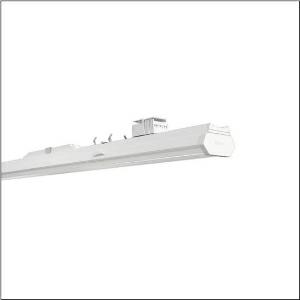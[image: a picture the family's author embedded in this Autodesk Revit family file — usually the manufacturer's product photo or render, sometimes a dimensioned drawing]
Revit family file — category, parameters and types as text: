
# Revit family: licross_r__11_protected_mo_51td12dn495g3s_4e23
name_source: partatom
category: Lighting Fixtures
units: mm (PartAtom-declared; Revit-internal decimal feet)

## family parameters
Cut with Voids When Loaded = No
Host = Face
Light Source = No
Part Type = Normal
Room Calculation Point = No
Round Connector Dimension = Use Diameter
Shared = No

## types (1)
- --- (1 x LED, 980 lm, 6.8 W, 4000K)
    Apparent Load = 7 VA
    CIE Flux Codes = 73 92 98 99 100
    Color Rendering = 80
    Color Temperature = 4000K
    Default Elevation = 1800 mm
    Description = Licross® 11 Protected MO, luminaire insert, of sheet steel, galvanised, coil coated, white, length: 1.500mm, width: 90mm, height: 101mm, LED rated luminous flux: 9.980lm, light colour: 840, control gear: DALI 2 (for two DALI lines), with plug, 6-pole, with phase selection, for trunking rail, 14-core, mains connection: 220..240V, AC, 50/60Hz, rated input power: 61W, for trunking rail, 14-core, halogen-free wiring, for emergency light function, converter,control gear: single battery element, battery: LiFePO4, 9Ah, primary light control with lens, of plastic, primary optical cover: cover, of PMMA, light emission: direct distribution, primary light characteristic: symmetric, protection rating (complete): IP54, insulation class (complete): insulation class I (protective earthing), certification: CE, UKCA, protection symbol: D if used in an environment with non-conductive dust loads with corresponding accessories, impact resistance: IK06, permissible ambient temperature for indoor applications: +5..+35°C, standard: EN 60598-2-22, LABS conformity tested according to VDMA 24364:2018-05, reducing of maximum allowable ambient temperature of 5°C with ceiling mounting, corresponds to IFS (International Featured Standards) requirements for safety and quality in the food industry, packaging unit: 1 piece
    Height = 92 mm
    Lamp = 1 x LED
    Lamp Light Flux = 980 lm
    Lamp Power = 6.8 W
    Lamp count = 1
    Length = 1500 mm
    Luminous efficacy = 144 lm/W
    Manufacturer = Siteco
    ModVariant = No
    Model = 51TD12DN495G3S
    Mounting Place = Ceiling
    Mounting Type = Pendant
    Number of Poles = 1
    OnlyDefault = Yes
    Power Factor = 1
    Product Name = Licross® 11 Protected MO
    Product group = luminaire insert
    ProductGroupID = 902
    Protection Class = Protection class I
    Protection Degree = IP 54
    RLX_Detail_Level = 1
    RLX_Emergency_Light_Flux = 0 lm
    RLX_Emergency_Type = 0
    RLX_Emergency_Type_DB = No
    RlxData = <blob elided: 24801 chars, md5=7ffff361>
    Socket = socket
    Standby Power = 0 W
    System Light Flux = 980 lm
    System Power = 7 W
    Type Comments = : emergency light operation: 3 h
    Type Image = l_1256145.jpg
    URL = http://relux.com
    VarID = @adj_090686
    Voltage = 0 V
    Weight = 0.00 kg
    Width = 88 mm

## geometry (parser evidence)
native form markers: Blend x4, Sweep x10
no freeform markers — native parametric forms only
